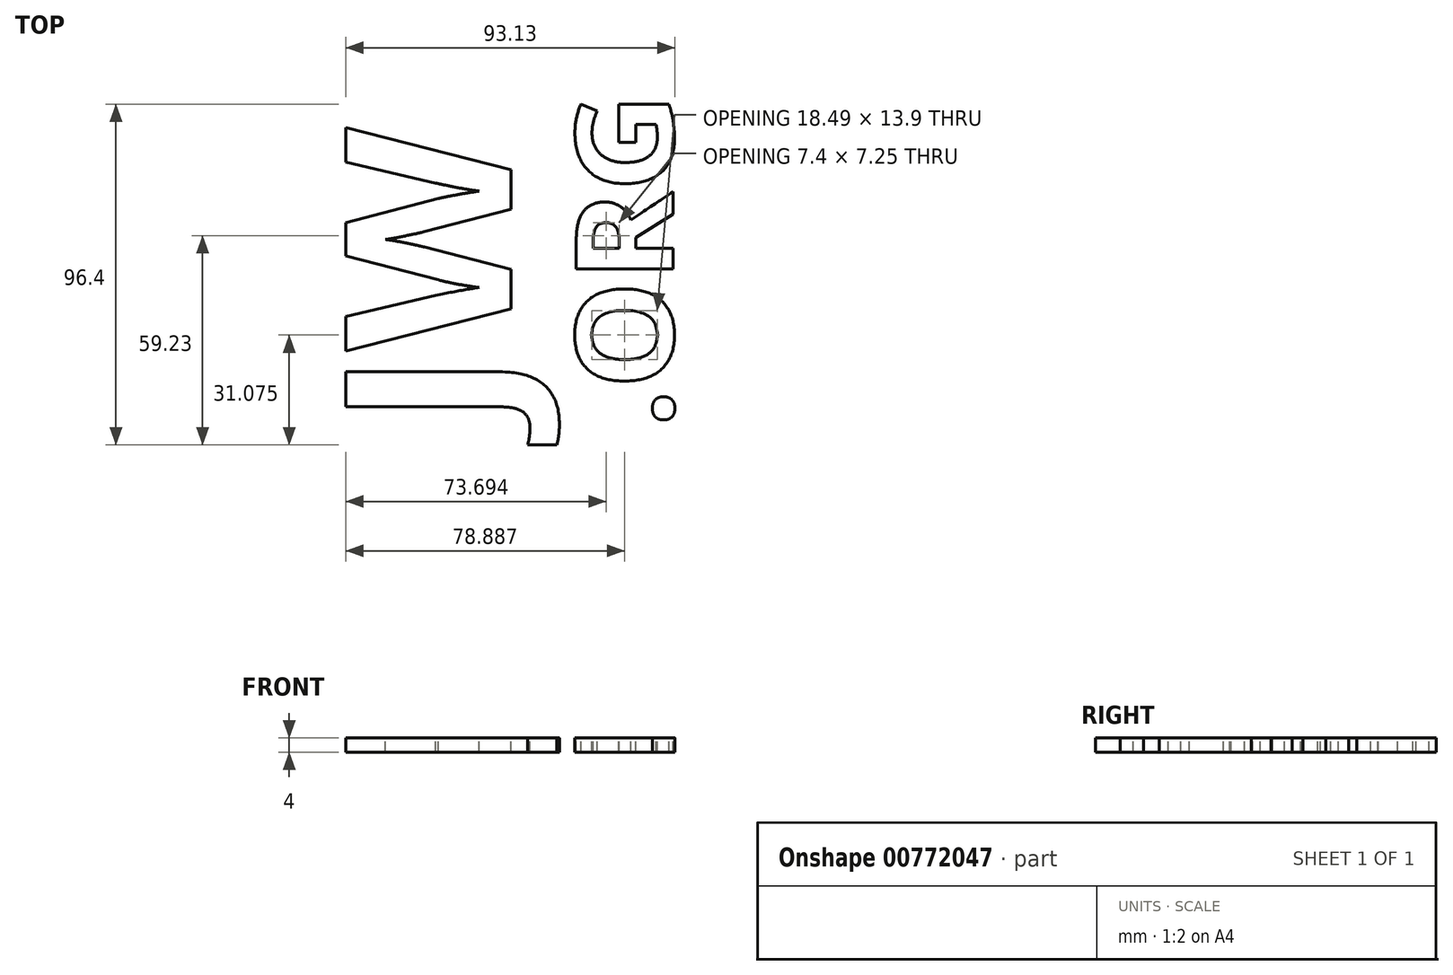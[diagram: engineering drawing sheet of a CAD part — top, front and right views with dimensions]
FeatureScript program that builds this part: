
annotation { "Feature Type Name" : "Feature", "Feature Type Description" : "" }
export const myFeature = defineFeature(function(context is Context, id is Id, definition is map)
    precondition{}
    {
        {
            var Q0;
            Q0=qCreatedBy(makeId("Top.planeOp"),FACE);
            var sketch = newSketch(context, id + "F0", { "sketchPlane" : qUnion([Q0])});
            skText(sketch, "E0", { "text": "JW", "fontName": "OpenSans-Bold.ttf"});
            skText(sketch, "E1", { "text": ".ORG", "fontName": "OpenSans-Bold.ttf"});
            const initialGuessF0  = {"E0": [0, -0.04702, 0, 1, 0.04711], "E1": [0.04592, -0.04702, 0, 1, 0.02763]};
            skSetInitialGuess(sketch, initialGuessF0);
            skSolve(sketch);
        }
        {
            var Q0;
            Q0=qSketchRegion(id+"F0",true);
            extrude(context, id + "F1", {"entities" : qUnion([Q0]), "oppositeDirection" : true, "depth" : 4 * mm, "offsetDistance" : 25 * mm});
        }
    });
